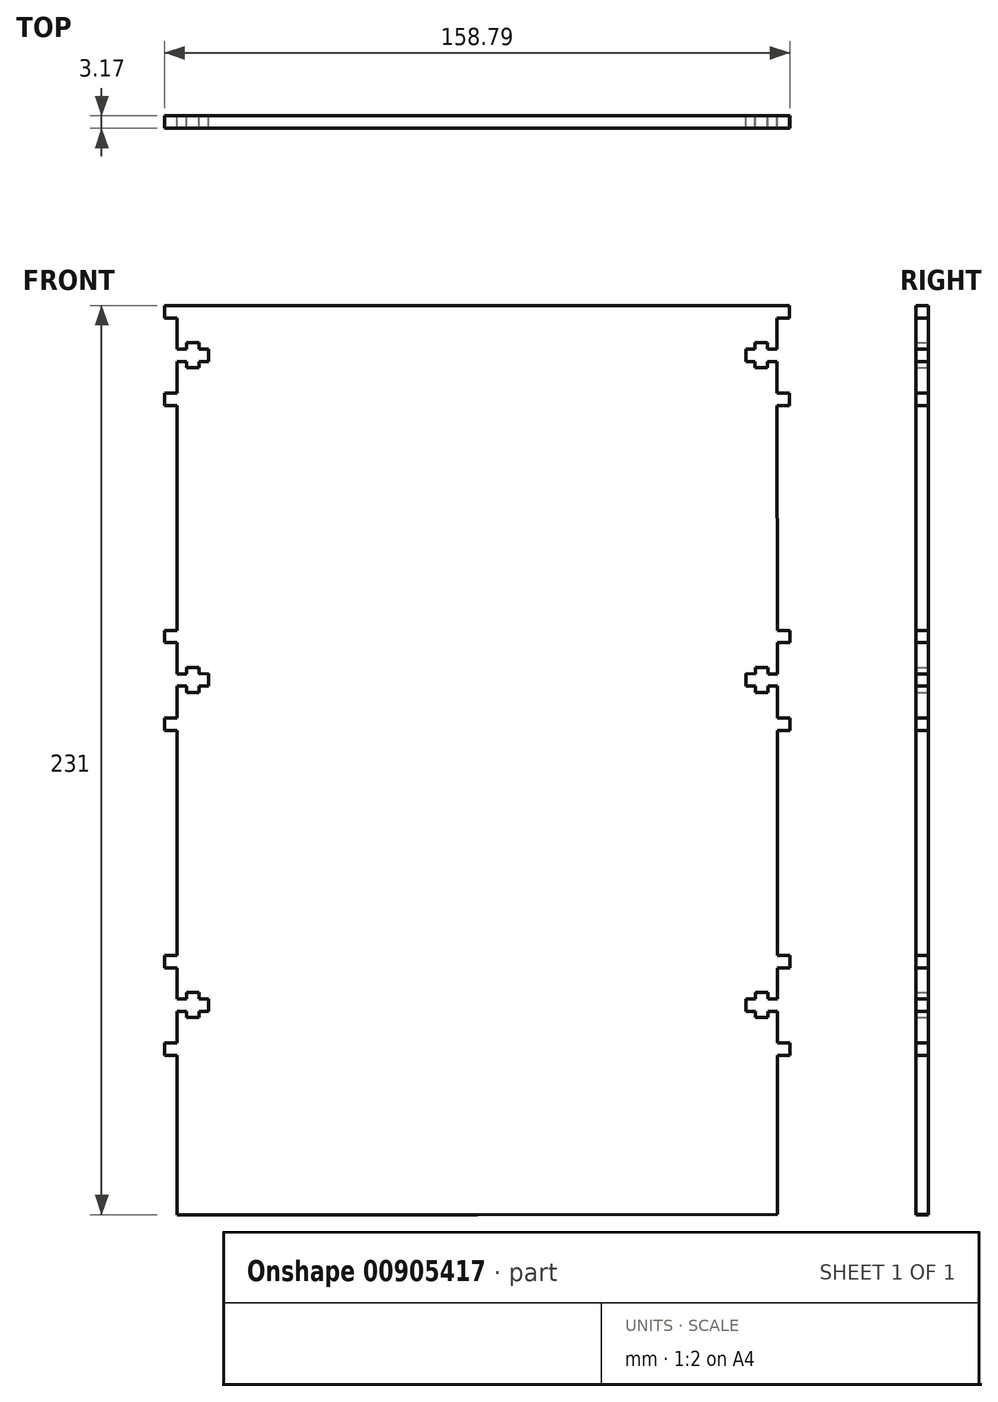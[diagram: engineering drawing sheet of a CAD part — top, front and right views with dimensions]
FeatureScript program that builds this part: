
annotation { "Feature Type Name" : "Feature", "Feature Type Description" : "" }
export const myFeature = defineFeature(function(context is Context, id is Id, definition is map)
    precondition{}
    {
        {
            var Q0;
            Q0=qCreatedBy(makeId("Front.planeOp"),FACE);
            var sketch = newSketch(context, id + "F0", { "sketchPlane" : qUnion([Q0])});
            skLineSegment(sketch, "E0", {"start": v(-79.4, 196.33) * mm, "end": v(-0.02, 196.33) * mm});
            skLineSegment(sketch, "E1", {"start": v(-79.4, 170.93) * mm, "end": v(-76.22, 170.93) * mm});
            skLineSegment(sketch, "E2", {"start": v(-76.22, 170.93) * mm, "end": v(-76.22, 113.78) * mm});
            skLineSegment(sketch, "E3", {"start": v(-76.22, 113.78) * mm, "end": v(-79.4, 113.78) * mm});
            skLineSegment(sketch, "E4", {"start": v(-79.4, 88.38) * mm, "end": v(-76.22, 88.38) * mm});
            skLineSegment(sketch, "E5", {"start": v(-76.22, 88.38) * mm, "end": v(-76.22, 31.23) * mm});
            skLineSegment(sketch, "E6", {"start": v(-76.22, 31.23) * mm, "end": v(-79.4, 31.23) * mm});
            skLineSegment(sketch, "E7", {"start": v(-79.4, 170.93) * mm, "end": v(-79.4, 174.1) * mm});
            skLineSegment(sketch, "E8", {"start": v(-79.4, 174.1) * mm, "end": v(-76.22, 174.1) * mm});
            skLineSegment(sketch, "E9", {"start": v(-79.4, 196.33) * mm, "end": v(-79.4, 193.15) * mm});
            skLineSegment(sketch, "E10", {"start": v(-79.4, 193.15) * mm, "end": v(-76.22, 193.15) * mm});
            skLineSegment(sketch, "E11", {"start": v(-76.22, 193.15) * mm, "end": v(-76.22, 185.24) * mm});
            skLineSegment(sketch, "E12", {"start": v(-76.22, 185.24) * mm, "end": v(-73.81, 185.24) * mm});
            skLineSegment(sketch, "E13", {"start": v(-73.81, 185.24) * mm, "end": v(-73.81, 186.85) * mm});
            skLineSegment(sketch, "E14", {"start": v(-73.81, 186.85) * mm, "end": v(-70.64, 186.85) * mm});
            skLineSegment(sketch, "E15", {"start": v(-70.64, 186.85) * mm, "end": v(-70.64, 185.24) * mm});
            skLineSegment(sketch, "E16", {"start": v(-70.64, 185.24) * mm, "end": v(-68.27, 185.29) * mm});
            skLineSegment(sketch, "E17", {"start": v(-76.22, 174.1) * mm, "end": v(-76.22, 182.11) * mm});
            skLineSegment(sketch, "E18", {"start": v(-76.22, 182.11) * mm, "end": v(-73.81, 182.11) * mm});
            skLineSegment(sketch, "E19", {"start": v(-73.81, 182.11) * mm, "end": v(-73.81, 180.5) * mm});
            skLineSegment(sketch, "E20", {"start": v(-73.81, 180.5) * mm, "end": v(-70.64, 180.5) * mm});
            skLineSegment(sketch, "E21", {"start": v(-70.64, 180.5) * mm, "end": v(-70.64, 182.11) * mm});
            skLineSegment(sketch, "E22", {"start": v(-70.64, 182.11) * mm, "end": v(-68.27, 182.11) * mm});
            skLineSegment(sketch, "E23", {"start": v(-68.27, 182.11) * mm, "end": v(-68.27, 185.29) * mm});
            skLineSegment(sketch, "E24", {"start": v(-79.4, 88.38) * mm, "end": v(-79.4, 91.55) * mm});
            skLineSegment(sketch, "E25", {"start": v(-79.4, 91.55) * mm, "end": v(-76.22, 91.55) * mm});
            skLineSegment(sketch, "E26", {"start": v(-79.4, 113.83) * mm, "end": v(-79.4, 110.65) * mm});
            skLineSegment(sketch, "E27", {"start": v(-79.4, 110.65) * mm, "end": v(-76.22, 110.65) * mm});
            skLineSegment(sketch, "E28", {"start": v(-76.22, 110.65) * mm, "end": v(-76.22, 102.74) * mm});
            skLineSegment(sketch, "E29", {"start": v(-76.22, 102.74) * mm, "end": v(-73.81, 102.74) * mm});
            skLineSegment(sketch, "E30", {"start": v(-73.81, 102.74) * mm, "end": v(-73.81, 104.35) * mm});
            skLineSegment(sketch, "E31", {"start": v(-73.81, 104.35) * mm, "end": v(-70.64, 104.35) * mm});
            skLineSegment(sketch, "E32", {"start": v(-70.64, 104.35) * mm, "end": v(-70.64, 102.74) * mm});
            skLineSegment(sketch, "E33", {"start": v(-70.64, 102.74) * mm, "end": v(-68.27, 102.8) * mm});
            skLineSegment(sketch, "E34", {"start": v(-76.22, 91.55) * mm, "end": v(-76.22, 99.62) * mm});
            skLineSegment(sketch, "E35", {"start": v(-76.22, 99.62) * mm, "end": v(-73.81, 99.62) * mm});
            skLineSegment(sketch, "E36", {"start": v(-73.81, 99.62) * mm, "end": v(-73.81, 98) * mm});
            skLineSegment(sketch, "E37", {"start": v(-73.81, 98) * mm, "end": v(-70.64, 98) * mm});
            skLineSegment(sketch, "E38", {"start": v(-70.64, 98) * mm, "end": v(-70.64, 99.62) * mm});
            skLineSegment(sketch, "E39", {"start": v(-70.64, 99.62) * mm, "end": v(-68.27, 99.62) * mm});
            skLineSegment(sketch, "E40", {"start": v(-68.27, 99.62) * mm, "end": v(-68.27, 102.8) * mm});
            skLineSegment(sketch, "E41", {"start": v(-79.4, 5.83) * mm, "end": v(-79.4, 9) * mm});
            skLineSegment(sketch, "E42", {"start": v(-79.4, 9) * mm, "end": v(-76.22, 9) * mm});
            skLineSegment(sketch, "E43", {"start": v(-79.4, 28.05) * mm, "end": v(-76.22, 28.05) * mm});
            skLineSegment(sketch, "E44", {"start": v(-76.22, 28.05) * mm, "end": v(-76.22, 20.14) * mm});
            skLineSegment(sketch, "E45", {"start": v(-76.22, 20.14) * mm, "end": v(-73.81, 20.14) * mm});
            skLineSegment(sketch, "E46", {"start": v(-73.81, 20.14) * mm, "end": v(-73.81, 21.75) * mm});
            skLineSegment(sketch, "E47", {"start": v(-73.81, 21.75) * mm, "end": v(-70.64, 21.75) * mm});
            skLineSegment(sketch, "E48", {"start": v(-70.64, 21.75) * mm, "end": v(-70.64, 20.14) * mm});
            skLineSegment(sketch, "E49", {"start": v(-70.64, 20.14) * mm, "end": v(-68.27, 20.19) * mm});
            skLineSegment(sketch, "E50", {"start": v(-76.22, 9) * mm, "end": v(-76.22, 17.01) * mm});
            skLineSegment(sketch, "E51", {"start": v(-76.22, 17.01) * mm, "end": v(-73.81, 17.01) * mm});
            skLineSegment(sketch, "E52", {"start": v(-73.81, 17.01) * mm, "end": v(-73.81, 15.4) * mm});
            skLineSegment(sketch, "E53", {"start": v(-73.81, 15.4) * mm, "end": v(-70.64, 15.4) * mm});
            skLineSegment(sketch, "E54", {"start": v(-70.64, 15.4) * mm, "end": v(-70.64, 17.01) * mm});
            skLineSegment(sketch, "E55", {"start": v(-70.64, 17.01) * mm, "end": v(-68.27, 17.01) * mm});
            skLineSegment(sketch, "E56", {"start": v(-68.27, 17.01) * mm, "end": v(-68.27, 20.19) * mm});
            skLineSegment(sketch, "E57", {"start": v(-79.4, 5.83) * mm, "end": v(-76.22, 5.83) * mm});
            skLineSegment(sketch, "E58", {"start": v(-76.22, 5.83) * mm, "end": v(-76.22, -34.66) * mm});
            skLineSegment(sketch, "E59", {"start": v(0, -34.66) * mm, "end": v(-0.02, 196.33) * mm});
            skLineSegment(sketch, "E60", {"start": v(-79.4, 28.05) * mm, "end": v(-79.4, 31.23) * mm});
            skLineSegment(sketch, "E61", {"start": v(-76.22, -34.66) * mm, "end": v(0, -34.66) * mm});
            skLineSegment(sketch, "E62.MirrorCS", {"start": v(70.62, 20.15) * mm, "end": v(68.26, 20.2) * mm});
            skLineSegment(sketch, "E63.MirrorCS", {"start": v(76.21, 17.03) * mm, "end": v(73.8, 17.03) * mm});
            skLineSegment(sketch, "E64.MirrorCS", {"start": v(70.59, 185.25) * mm, "end": v(68.23, 185.3) * mm});
            skLineSegment(sketch, "E65.MirrorCS", {"start": v(70.63, 15.42) * mm, "end": v(70.63, 17.03) * mm});
            skLineSegment(sketch, "E66.MirrorCS", {"start": v(70.63, 17.03) * mm, "end": v(68.26, 17.03) * mm});
            skLineSegment(sketch, "E67.MirrorCS", {"start": v(76.21, 20.16) * mm, "end": v(73.8, 20.15) * mm});
            skLineSegment(sketch, "E68.MirrorCS", {"start": v(70.6, 102.76) * mm, "end": v(68.25, 102.8) * mm});
            skLineSegment(sketch, "E69.MirrorCS", {"start": v(73.76, 185.25) * mm, "end": v(73.76, 186.87) * mm});
            skLineSegment(sketch, "E70.MirrorCS", {"start": v(76.18, 182.13) * mm, "end": v(73.77, 182.13) * mm});
            skLineSegment(sketch, "E71.MirrorCS", {"start": v(76.21, 31.24) * mm, "end": v(79.39, 31.24) * mm});
            skLineSegment(sketch, "E72.MirrorCS", {"start": v(73.8, 21.77) * mm, "end": v(70.62, 21.77) * mm});
            skLineSegment(sketch, "E73.MirrorCS", {"start": v(68.26, 17.03) * mm, "end": v(68.26, 20.2) * mm});
            skLineSegment(sketch, "E74.MirrorCS", {"start": v(76.2, 102.76) * mm, "end": v(73.78, 102.76) * mm});
            skLineSegment(sketch, "E75.MirrorCS", {"start": v(70.59, 186.87) * mm, "end": v(70.59, 185.25) * mm});
            skLineSegment(sketch, "E76.MirrorCS", {"start": v(79.39, 28.07) * mm, "end": v(76.21, 28.07) * mm});
            skLineSegment(sketch, "E77.MirrorCS", {"start": v(76.21, 28.07) * mm, "end": v(76.21, 20.16) * mm});
            skLineSegment(sketch, "E78.MirrorCS", {"start": v(73.8, 17.03) * mm, "end": v(73.8, 15.42) * mm});
            skLineSegment(sketch, "E79.MirrorCS", {"start": v(79.39, 28.07) * mm, "end": v(79.39, 31.24) * mm});
            skLineSegment(sketch, "E80.MirrorCS", {"start": v(76.2, 99.63) * mm, "end": v(73.78, 99.63) * mm});
            skLineSegment(sketch, "E81.MirrorCS", {"start": v(73.8, 20.15) * mm, "end": v(73.8, 21.77) * mm});
            skLineSegment(sketch, "E82.MirrorCS", {"start": v(70.6, 98.02) * mm, "end": v(70.6, 99.63) * mm});
            skLineSegment(sketch, "E83.MirrorCS", {"start": v(70.6, 182.13) * mm, "end": v(68.23, 182.13) * mm});
            skLineSegment(sketch, "E84.MirrorCS", {"start": v(73.8, 15.42) * mm, "end": v(70.63, 15.42) * mm});
            skLineSegment(sketch, "E85.MirrorCS", {"start": v(70.62, 21.77) * mm, "end": v(70.62, 20.15) * mm});
            skLineSegment(sketch, "E86.MirrorCS", {"start": v(73.76, 186.87) * mm, "end": v(70.59, 186.87) * mm});
            skLineSegment(sketch, "E87.MirrorCS", {"start": v(76.2, 113.8) * mm, "end": v(79.37, 113.8) * mm});
            skLineSegment(sketch, "E88.MirrorCS", {"start": v(79.37, 110.67) * mm, "end": v(76.2, 110.67) * mm});
            skLineSegment(sketch, "E89.MirrorCS", {"start": v(76.2, 91.57) * mm, "end": v(76.2, 99.63) * mm});
            skLineSegment(sketch, "E90.MirrorCS", {"start": v(79.4, 9.02) * mm, "end": v(76.22, 9.02) * mm});
            skLineSegment(sketch, "E91.MirrorCS", {"start": v(76.22, 9.02) * mm, "end": v(76.21, 17.03) * mm});
            skLineSegment(sketch, "E92.MirrorCS", {"start": v(79.35, 193.17) * mm, "end": v(76.18, 193.17) * mm});
            skLineSegment(sketch, "E93.MirrorCS", {"start": v(79.35, 196.34) * mm, "end": v(79.35, 193.17) * mm});
            skLineSegment(sketch, "E94.MirrorCS", {"start": v(79.37, 91.57) * mm, "end": v(76.2, 91.57) * mm});
            skLineSegment(sketch, "E95.MirrorCS", {"start": v(70.6, 104.37) * mm, "end": v(70.6, 102.76) * mm});
            skLineSegment(sketch, "E96.MirrorCS", {"start": v(79.37, 88.4) * mm, "end": v(76.2, 88.4) * mm});
            skLineSegment(sketch, "E97.MirrorCS", {"start": v(68.23, 182.13) * mm, "end": v(68.23, 185.3) * mm});
            skLineSegment(sketch, "E98.MirrorCS", {"start": v(73.78, 99.63) * mm, "end": v(73.78, 98.02) * mm});
            skLineSegment(sketch, "E99.MirrorCS", {"start": v(73.78, 104.37) * mm, "end": v(70.6, 104.37) * mm});
            skLineSegment(sketch, "E100.MirrorCS", {"start": v(73.78, 102.76) * mm, "end": v(73.78, 104.37) * mm});
            skLineSegment(sketch, "E101.MirrorCS", {"start": v(79.37, 113.84) * mm, "end": v(79.37, 110.67) * mm});
            skLineSegment(sketch, "E102.MirrorCS", {"start": v(70.6, 180.52) * mm, "end": v(70.6, 182.13) * mm});
            skLineSegment(sketch, "E103.MirrorCS", {"start": v(76.18, 193.17) * mm, "end": v(76.18, 185.26) * mm});
            skLineSegment(sketch, "E104.MirrorCS", {"start": v(76.2, 110.67) * mm, "end": v(76.2, 102.76) * mm});
            skLineSegment(sketch, "E105.MirrorCS", {"start": v(79.37, 88.4) * mm, "end": v(79.37, 91.57) * mm});
            skLineSegment(sketch, "E106.MirrorCS", {"start": v(73.77, 182.13) * mm, "end": v(73.77, 180.52) * mm});
            skLineSegment(sketch, "E107.MirrorCS", {"start": v(76.18, 185.26) * mm, "end": v(73.76, 185.25) * mm});
            skLineSegment(sketch, "E108.MirrorCS", {"start": v(68.25, 99.63) * mm, "end": v(68.25, 102.8) * mm});
            skLineSegment(sketch, "E109.MirrorCS", {"start": v(73.77, 180.52) * mm, "end": v(70.6, 180.52) * mm});
            skLineSegment(sketch, "E110.MirrorCS", {"start": v(70.6, 99.63) * mm, "end": v(68.25, 99.63) * mm});
            skLineSegment(sketch, "E111.MirrorCS", {"start": v(73.78, 98.02) * mm, "end": v(70.6, 98.02) * mm});
            skLineSegment(sketch, "E112.MirrorCS", {"start": v(79.36, 174.12) * mm, "end": v(76.18, 174.12) * mm});
            skLineSegment(sketch, "E113.MirrorCS", {"start": v(76.18, 174.12) * mm, "end": v(76.18, 182.13) * mm});
            skLineSegment(sketch, "E114.MirrorCS", {"start": v(79.4, 5.84) * mm, "end": v(79.4, 9.02) * mm});
            skLineSegment(sketch, "E115.MirrorCS", {"start": v(79.4, 5.84) * mm, "end": v(76.22, 5.84) * mm});
            skLineSegment(sketch, "E116.MirrorCS", {"start": v(79.36, 170.94) * mm, "end": v(79.36, 174.12) * mm});
            skLineSegment(sketch, "E117.MirrorCS", {"start": v(79.36, 170.94) * mm, "end": v(76.18, 170.94) * mm});
            skLineSegment(sketch, "E118.MirrorCS", {"start": v(76.22, 5.84) * mm, "end": v(76.22, -34.65) * mm});
            skLineSegment(sketch, "E119.MirrorCS", {"start": v(76.2, 88.4) * mm, "end": v(76.21, 31.24) * mm});
            skLineSegment(sketch, "E120.MirrorCS", {"start": v(79.35, 196.34) * mm, "end": v(-0.02, 196.33) * mm});
            skLineSegment(sketch, "E121.MirrorCS", {"start": v(76.18, 170.94) * mm, "end": v(76.2, 113.8) * mm});
            skLineSegment(sketch, "E122.MirrorCS", {"start": v(76.22, -34.65) * mm, "end": v(0, -34.66) * mm});
            skSolve(sketch);
        }
        {
            var Q0;
            Q0 = qSketchRegion(id + "F0", true);
            extrude(context, id + "F1", {"entities" : qUnion([Q0]), "depth" : 3.17 * mm, "offsetDistance" : 25.4 * mm});
        }
    });
